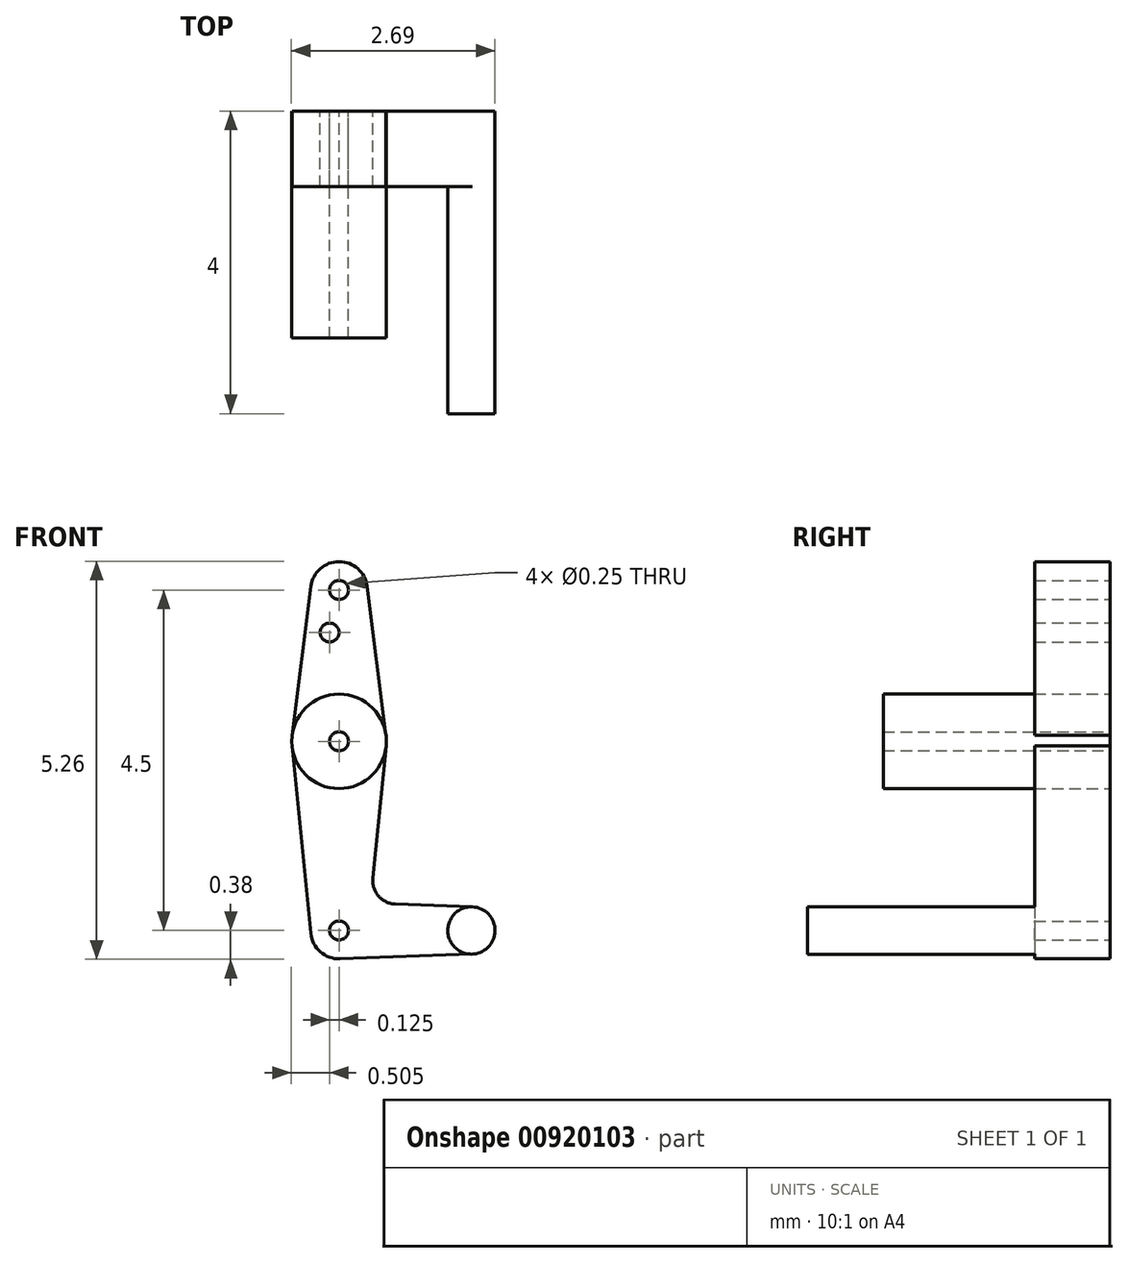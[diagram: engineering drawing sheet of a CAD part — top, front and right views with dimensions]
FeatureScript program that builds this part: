
annotation { "Feature Type Name" : "Feature", "Feature Type Description" : "" }
export const myFeature = defineFeature(function(context is Context, id is Id, definition is map)
    precondition{}
    {
        {
            var Q0;
            Q0=qCreatedBy(makeId("Front.planeOp"),FACE);
            var sketch = newSketch(context, id + "F0", { "sketchPlane" : qUnion([Q0])});
            skLineSegment(sketch, "E0", {"start": v(0, 0) * mm, "end": v(1.75, 0) * mm});
            skCircle(sketch, "E1", {"center": v(0, 2.5) * mm, "radius": 0.62 * mm});
            skCircle(sketch, "E2", {"center": v(0, 0) * mm, "radius": 0.38 * mm});
            skCircle(sketch, "E3", {"center": v(1.75, 0) * mm, "radius": 0.31 * mm});
            skLineSegment(sketch, "E4", {"start": v(0, 0) * mm, "end": v(0, 4.5) * mm});
            skCircle(sketch, "E5", {"center": v(0, 4.5) * mm, "radius": 0.38 * mm});
            skLineSegment(sketch, "E6", {"start": v(-0.37, 4.55) * mm, "end": v(-0.62, 2.58) * mm});
            skLineSegment(sketch, "E7", {"start": v(0.37, 4.55) * mm, "end": v(0.62, 2.58) * mm});
            skLineSegment(sketch, "E8", {"start": v(-0.62, 2.44) * mm, "end": v(-0.37, -0.04) * mm});
            skLineSegment(sketch, "E9", {"start": v(0.62, 2.44) * mm, "end": v(0.45, 0.7) * mm});
            skLineSegment(sketch, "E10", {"start": v(0.75, 0.35) * mm, "end": v(1.76, 0.31) * mm});
            skPoint(sketch, "E11.orphan", {"position": v(-0.38, 0) * mm});
            skLineSegment(sketch, "E12", {"start": v(0.01, -0.37) * mm, "end": v(1.76, -0.31) * mm});
            skCircle(sketch, "E13", {"center": v(-0.12, 3.94) * mm, "radius": 0.12 * mm});
            skCircle(sketch, "E14", {"center": v(0, 4.5) * mm, "radius": 0.12 * mm});
            skCircle(sketch, "E15", {"center": v(0, 2.5) * mm, "radius": 0.12 * mm});
            skCircle(sketch, "E16", {"center": v(0, 0) * mm, "radius": 0.12 * mm});
            skCircle(sketch, "E17", {"center": v(1.75, 0) * mm, "radius": 0.12 * mm});
            skPoint(sketch, "E18.newPointA", {"position": v(0.38, 0) * mm});
            skArc(sketch, "E18.filletArc", {"start": v(0.45, 0.7) * mm, "mid": v(0.52, 0.46) * mm, "end": v(0.75, 0.35) * mm});
            skSolve(sketch);
        }
        {
            var Q0;
            {var subQ5=sQuery(id+"F0.wireOp",EDGE,"E12");Q0=makeQuery(id+"F0.imprint","IMPRINT",FACE,{"disambiguationData":[TD([[makeQuery(id+"F0.imprint","IMPRINT",EDGE,{"derivedFrom":subQ5}),1.0]])]});}
            var Q1;
            {var subQ0=sQuery(id+"F0.wireOp",EDGE,"E7");Q1=makeQuery(id+"F0.imprint","IMPRINT",FACE,{"disambiguationData":[TD([[makeQuery(id+"F0.imprint","IMPRINT",EDGE,{"derivedFrom":subQ0}),-1.0]])]});}
            var Q2;
            {var subQ2=sQuery(id+"F0.wireOp",EDGE,"E0");var subQ4=sQuery(id+"F0.wireOp",EDGE,"E16");var subQ5=makeQuery(id+"F0.imprint","INTERSECT",VERTEX,{"derivedFrom":[subQ2,subQ4]});Q2=makeQuery(id+"F0.imprint","IMPRINT",FACE,{"disambiguationData":[TD([[makeQuery(id+"F0.imprint","IMPRINT",EDGE,{"disambiguationData":[TD([[subQ5,-1.0]])],"derivedFrom":subQ2}),-1.0]])]});}
            var Q3;
            {var subQ0=sQuery(id+"F0.wireOp",EDGE,"E6");Q3=makeQuery(id+"F0.imprint","IMPRINT",FACE,{"disambiguationData":[TD([[makeQuery(id+"F0.imprint","IMPRINT",EDGE,{"derivedFrom":subQ0}),1.0]])]});}
            var Q4;
            {var subQ8=sQuery(id+"F0.wireOp",EDGE,"E9");Q4=makeQuery(id+"F0.imprint","IMPRINT",FACE,{"disambiguationData":[TD([[makeQuery(id+"F0.imprint","IMPRINT",EDGE,{"derivedFrom":subQ8}),-1.0]])]});}
            var Q5;
            {var subQ0=sQuery(id+"F0.wireOp",EDGE,"E8");Q5=makeQuery(id+"F0.imprint","IMPRINT",FACE,{"disambiguationData":[TD([[makeQuery(id+"F0.imprint","IMPRINT",EDGE,{"derivedFrom":subQ0}),1.0]])]});}
            var Q6;
            Q6=makeQuery(id+"F0.imprint","IMPRINT",FACE,{"disambiguationData":[TD([[makeQuery(id+"F0.imprint","IMPRINT",EDGE,{"derivedFrom":sQuery(id+"F0.wireOp",EDGE,"E14")}),-1.0]])]});
            var Q7;
            {var subQ0=sQuery(id+"F0.wireOp",EDGE,"E16");var subQ1=sQuery(id+"F0.wireOp",EDGE,"E0");var subQ2=makeQuery(id+"F0.imprint","INTERSECT",VERTEX,{"derivedFrom":[subQ1,subQ0]});Q7=makeQuery(id+"F0.imprint","IMPRINT",FACE,{"disambiguationData":[TD([[makeQuery(id+"F0.imprint","IMPRINT",EDGE,{"disambiguationData":[TD([[subQ2,-1.0]])],"derivedFrom":subQ1}),1.0]])]});}
            extrude(context, id + "F1", {"entities" : qUnion([Q0, Q1, Q2, Q3, Q4, Q5, Q6, Q7]), "depth" : 1 * mm, "offsetDistance" : 25 * mm});
        }
        {
            var Q0;
            {var subQ1=sQuery(id+"F0.wireOp",EDGE,"E1");var subQ5=makeQuery(id+"F0.imprint","INTERSECT",VERTEX,{"derivedFrom":[subQ1,sQuery(id+"F0.wireOp",EDGE,"E7")]});Q0=makeQuery(id+"F0.imprint","IMPRINT",FACE,{"disambiguationData":[TD([[makeQuery(id+"F0.imprint","IMPRINT",EDGE,{"disambiguationData":[TD([[subQ5,-1.0]])],"derivedFrom":subQ1}),1.0]])]});}
            var Q1;
            {var subQ0=sQuery(id+"F0.wireOp",EDGE,"E1");var subQ4=makeQuery(id+"F0.imprint","INTERSECT",VERTEX,{"derivedFrom":[subQ0,sQuery(id+"F0.wireOp",EDGE,"E6")]});Q1=makeQuery(id+"F0.imprint","IMPRINT",FACE,{"disambiguationData":[TD([[makeQuery(id+"F0.imprint","IMPRINT",EDGE,{"disambiguationData":[TD([[subQ4,1.0]])],"derivedFrom":subQ0}),1.0]])]});}
            extrude(context, id + "F2", {"entities" : qUnion([Q0, Q1]), "depth" : 3 * mm, "offsetDistance" : 25 * mm});
        }
        {
            var Q0;
            Q0=makeQuery(id+"F0.imprint","IMPRINT",FACE,{"disambiguationData":[TD([[makeQuery(id+"F0.imprint","IMPRINT",EDGE,{"derivedFrom":sQuery(id+"F0.wireOp",EDGE,"E17")}),-1.0]])]});
            var Q1;
            Q1=makeQuery(id+"F0.imprint","IMPRINT",FACE,{"disambiguationData":[TD([[makeQuery(id+"F0.imprint","IMPRINT",EDGE,{"derivedFrom":sQuery(id+"F0.wireOp",EDGE,"E17")}),1.0]])]});
            extrude(context, id + "F3", {"entities" : qUnion([Q0, Q1]), "operationType" : NewBodyOperationType.ADD, "depth" : 4 * mm, "offsetDistance" : 25 * mm});
        }
    });
